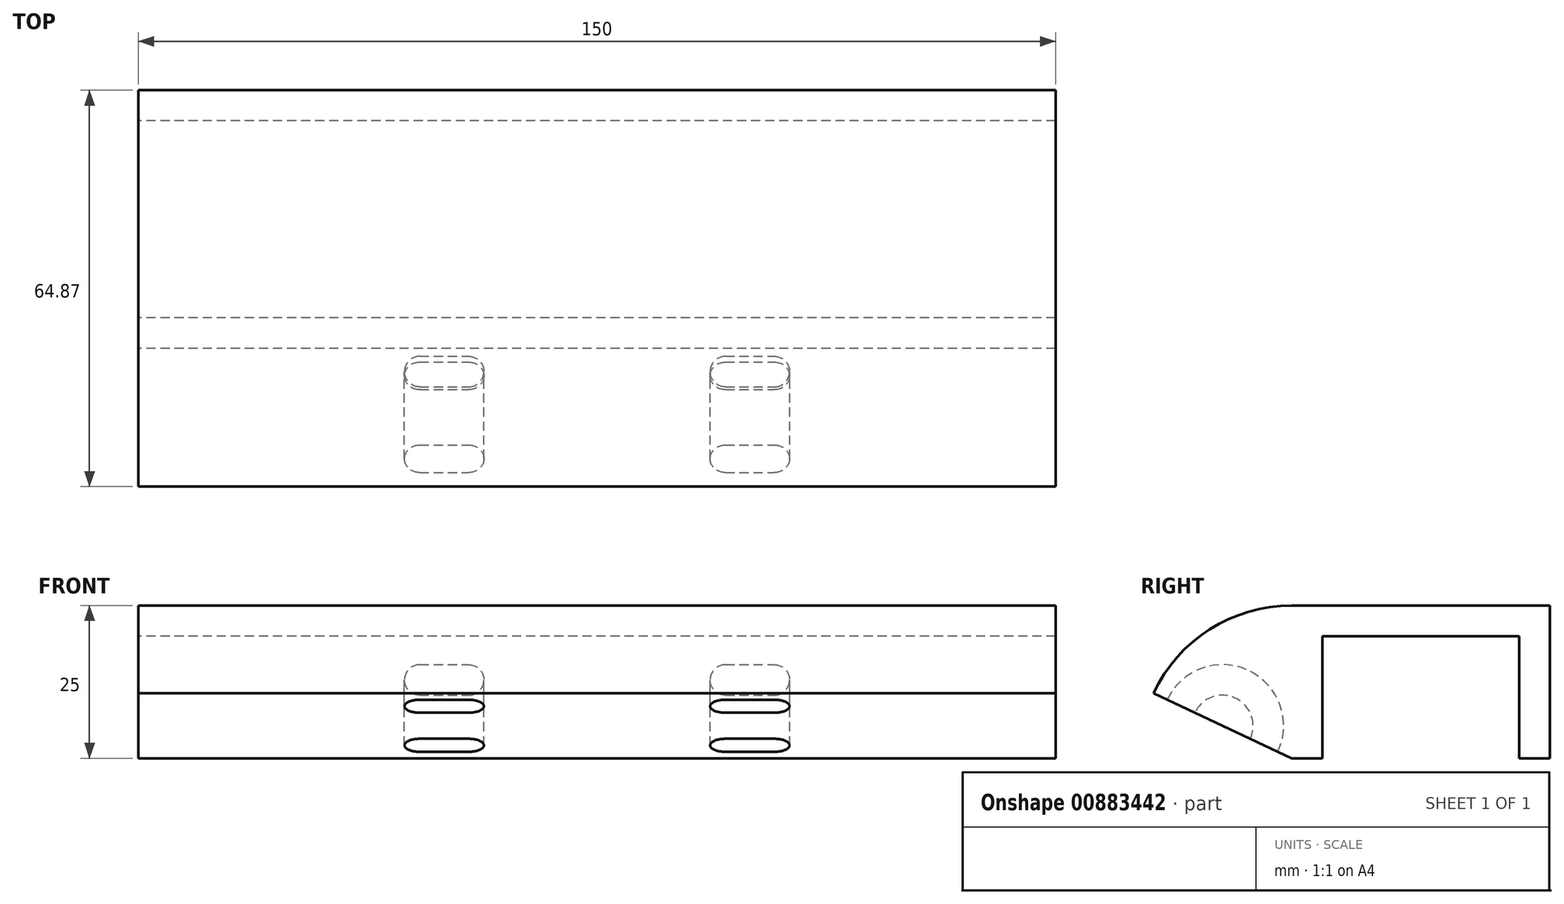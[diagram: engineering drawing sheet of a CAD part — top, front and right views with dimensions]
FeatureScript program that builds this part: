
annotation { "Feature Type Name" : "Feature", "Feature Type Description" : "" }
export const myFeature = defineFeature(function(context is Context, id is Id, definition is map)
    precondition{}
    {
        {
            var Q0;
            Q0=qCreatedBy(makeId("Right.planeOp"),FACE);
            var sketch = newSketch(context, id + "F0", { "sketchPlane" : qUnion([Q0])});
            skLineSegment(sketch, "E0.bottom", {"start": v(-16.12, 10) * mm, "end": v(16.13, 10) * mm});
            skLineSegment(sketch, "E0.top", {"start": v(-16.13, -10) * mm, "end": v(16.12, -10) * mm});
            skLineSegment(sketch, "E0.left", {"start": v(-16.12, 10) * mm, "end": v(-16.13, -10) * mm});
            skLineSegment(sketch, "E0.right", {"start": v(16.13, 10) * mm, "end": v(16.12, -10) * mm});
            skLineSegment(sketch, "E1", {"start": v(-16.12, 10) * mm, "end": v(16.13, -10) * mm, "construction": true});
            skLineSegment(sketch, "E2", {"start": v(16.13, 10) * mm, "end": v(-16.13, -10) * mm, "construction": true});
            skPoint(sketch, "E3", {"position": v(0, 0) * mm});
            skPoint(sketch, "E4.oppositeSnap0", {"position": v(0, -10) * mm});
            skLineSegment(sketch, "E4.bottom", {"start": v(-21.13, 15) * mm, "end": v(21.13, 15) * mm});
            skLineSegment(sketch, "E4.top", {"start": v(-21.13, -10) * mm, "end": v(21.12, -10) * mm});
            skLineSegment(sketch, "E4.left", {"start": v(-21.13, 15) * mm, "end": v(-21.13, -10) * mm});
            skLineSegment(sketch, "E4.right", {"start": v(21.13, 15) * mm, "end": v(21.12, -10) * mm});
            skLineSegment(sketch, "E5", {"start": v(-21.12, -10) * mm, "end": v(-43.75, 0.64) * mm});
            skArc(sketch, "E6.trimOffspring", {"start": v(-21.13, 15) * mm, "mid": v(-34.52, 11.1) * mm, "end": v(-43.75, 0.64) * mm});
            skLineSegment(sketch, "E7", {"start": v(-21.13, -10) * mm, "end": v(-224.33, -441.8) * mm, "construction": true});
            skSolve(sketch);
        }
        {
            var Q0;
            Q0=makeQuery(id+"F0.imprint","IMPRINT",FACE,{"disambiguationData":[TD([[makeQuery(id+"F0.imprint","IMPRINT",EDGE,{"derivedFrom":sQuery(id+"F0.wireOp",EDGE,"E4.left")}),-1.0]])]});
            var Q1;
            Q1=makeQuery(id+"F0.imprint","IMPRINT",FACE,{"disambiguationData":[TD([[makeQuery(id+"F0.imprint","IMPRINT",EDGE,{"derivedFrom":sQuery(id+"F0.wireOp",EDGE,"E0.bottom")}),1.0]])]});
            extrude(context, id + "F1", {"entities" : qUnion([Q0, Q1]), "depth" : 150 * mm, "offsetDistance" : 25 * mm});
        }
        {
            var Q0;
            Q0=makeQuery(id+"F1.opExtrude","SWEPT_FACE",FACE,{"disambiguationData":[OSD([sQuery(id+"F0.wireOp",EDGE,"E5")])]});
            var sketch = newSketch(context, id + "F2", { "sketchPlane" : qUnion([Q0])});
            skLineSegment(sketch, "E8", {"start": v(50, 39.86) * mm, "end": v(50, 14.86) * mm, "construction": true});
            skLineSegment(sketch, "E9", {"start": v(0, 27.36) * mm, "end": v(150, 27.36) * mm, "construction": true});
            skLineSegment(sketch, "E10", {"start": v(100, 39.86) * mm, "end": v(100, 14.86) * mm, "construction": true});
            skArc(sketch, "E11", {"start": v(46, 37.36) * mm, "mid": v(43.5, 34.86) * mm, "end": v(46, 32.36) * mm});
            skArc(sketch, "E12", {"start": v(54, 32.36) * mm, "mid": v(56.5, 34.86) * mm, "end": v(54, 37.36) * mm});
            skLineSegment(sketch, "E13", {"start": v(46, 34.86) * mm, "end": v(54, 34.86) * mm, "construction": true});
            skLineSegment(sketch, "E14", {"start": v(46, 37.36) * mm, "end": v(54, 37.36) * mm});
            skLineSegment(sketch, "E15", {"start": v(46, 32.36) * mm, "end": v(54, 32.36) * mm});
            skPoint(sketch, "E16", {"position": v(50, 34.86) * mm});
            skArc(sketch, "E17", {"start": v(46, 22.36) * mm, "mid": v(43.5, 19.86) * mm, "end": v(46, 17.36) * mm});
            skArc(sketch, "E18", {"start": v(54, 17.36) * mm, "mid": v(56.5, 19.86) * mm, "end": v(54, 22.36) * mm});
            skLineSegment(sketch, "E19", {"start": v(46, 19.86) * mm, "end": v(54, 19.86) * mm, "construction": true});
            skLineSegment(sketch, "E20", {"start": v(46, 22.36) * mm, "end": v(54, 22.36) * mm});
            skLineSegment(sketch, "E21", {"start": v(46, 17.36) * mm, "end": v(54, 17.36) * mm});
            skPoint(sketch, "E22", {"position": v(50, 19.86) * mm});
            skPoint(sketch, "E23", {"position": v(50, 27.36) * mm});
            skArc(sketch, "E24", {"start": v(96, 22.36) * mm, "mid": v(93.5, 19.86) * mm, "end": v(96, 17.36) * mm});
            skArc(sketch, "E25", {"start": v(104, 17.36) * mm, "mid": v(106.5, 19.86) * mm, "end": v(104, 22.36) * mm});
            skLineSegment(sketch, "E26", {"start": v(96, 19.86) * mm, "end": v(104, 19.86) * mm, "construction": true});
            skLineSegment(sketch, "E27", {"start": v(96, 22.36) * mm, "end": v(104, 22.36) * mm});
            skLineSegment(sketch, "E28", {"start": v(96, 17.36) * mm, "end": v(104, 17.36) * mm});
            skPoint(sketch, "E29", {"position": v(100, 19.86) * mm});
            skSolve(sketch);
        }
        {
            var Q0;
            Q0=makeQuery(id+"F2.imprint","IMPRINT",FACE,{"disambiguationData":[TD([[makeQuery(id+"F2.imprint","IMPRINT",EDGE,{"derivedFrom":sQuery(id+"F2.wireOp",EDGE,"E17")}),1.0]])]});
            var Q1;
            Q1=makeQuery(id+"F2.imprint","IMPRINT",FACE,{"disambiguationData":[TD([[makeQuery(id+"F2.imprint","IMPRINT",EDGE,{"derivedFrom":sQuery(id+"F2.wireOp",EDGE,"E24")}),1.0]])]});
            var Q2;
            Q2=sQuery(id+"F2.wireOp",EDGE,"E9");
            revolve(context, id + "F3", {"operationType" : NewBodyOperationType.REMOVE, "surfaceOperationType" : NewSurfaceOperationType.NEW, "entities" : qUnion([Q0, Q1]), "axis" : qUnion([Q2]), "revolveType" : RevolveType.FULL, "oppositeDirection" : true});
        }
    });
